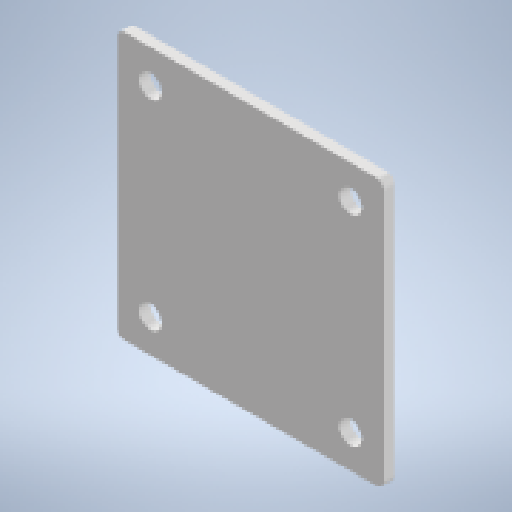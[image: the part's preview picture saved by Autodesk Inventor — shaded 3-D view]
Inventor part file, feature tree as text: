
AUTODESK INVENTOR PART (.ipt)
format: ipt  version: 2025 (Build 290162010, 162A)  size: 156,672 bytes
history: native  units: mm
features: sketch x2, sheet_metal_op x1, hole x1, chamfer x1, mirror x1, other x1
ambient origin geometry x8: Origin, YZ Plane, XZ Plane, XY Plane, X Axis, Y Axis, Z Axis, Center Point
bodies: Solid1 (feature_tree)
feature tree (7):
  sheet_metal_op  "Face1"
  hole  "Hole1"  [1 undecoded]
  chamfer  "Corner Round1"
  mirror  "Mirror1"
  sketch  "Sketch1"  dims[d0=200.0mm d1=170.0mm]
  other  "Plate1"
  sketch  "Sketch2"  dims[d2=8.0mm d3=17.0mm d4=6.0mm d5=4.0mm d6=2.0mm d7=90.0deg d8=8.0mm d9=20.594885mm d10=20.0mm d12=20.0mm d13=6.0mm]
note: 1 required parameter value undecoded (feature->parameter linkage not recoverable at this tier; creation-order binding heuristic only, values carry confidence <= 0.55)
